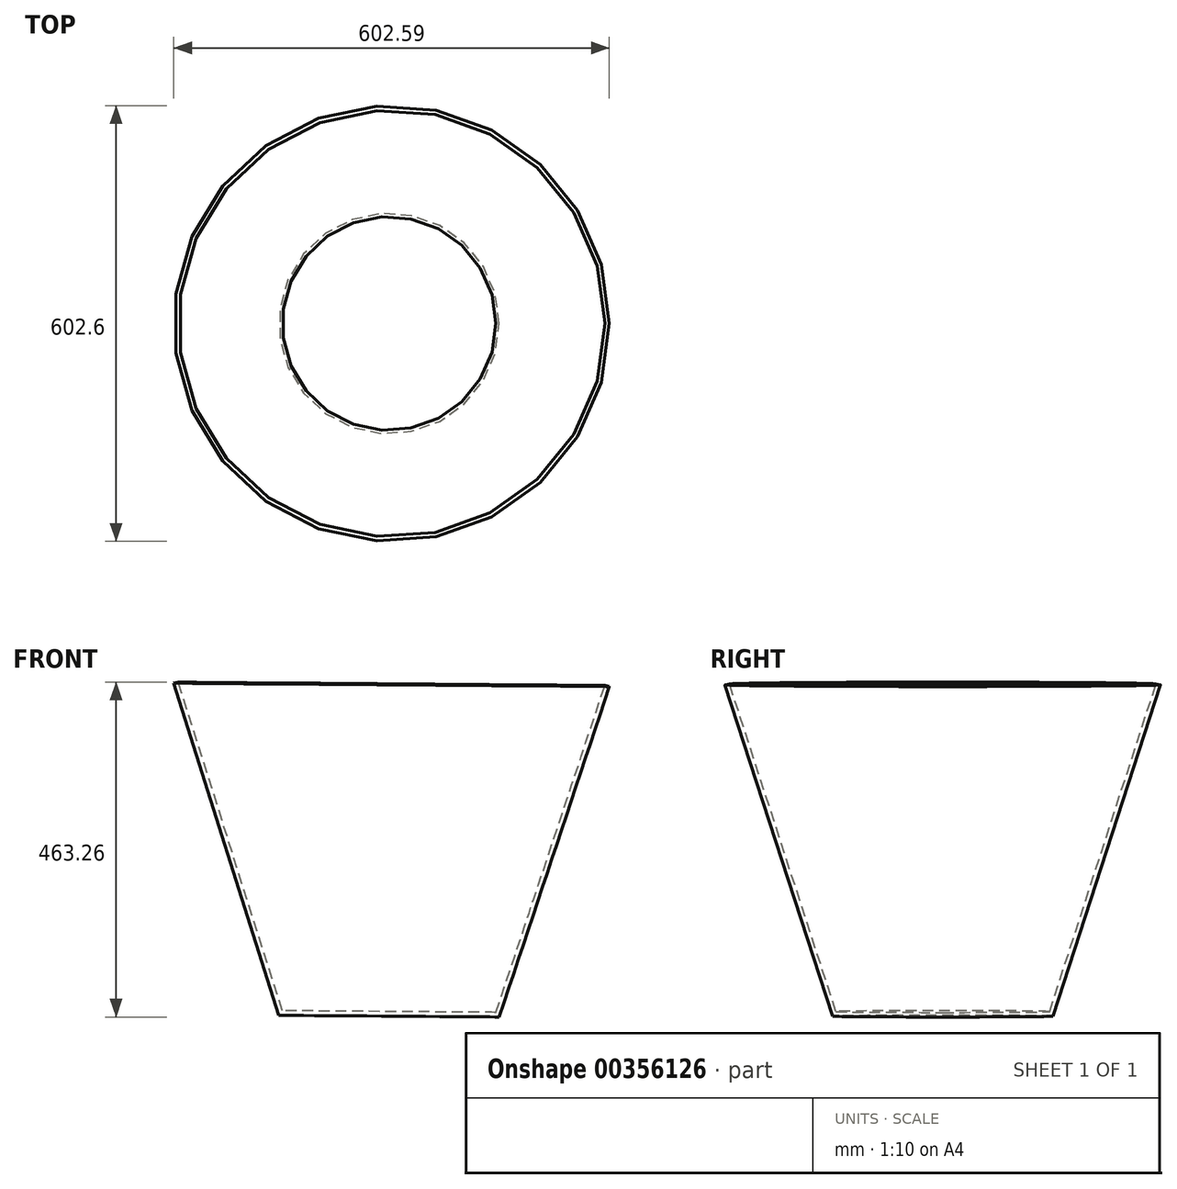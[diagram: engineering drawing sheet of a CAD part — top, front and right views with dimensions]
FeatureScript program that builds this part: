
annotation { "Feature Type Name" : "Feature", "Feature Type Description" : "" }
export const myFeature = defineFeature(function(context is Context, id is Id, definition is map)
    precondition{}
    {
        {
            var Q0;
            Q0=qCreatedBy(makeId("Front.planeOp"),FACE);
            var sketch = newSketch(context, id + "F0", { "sketchPlane" : qUnion([Q0])});
            skLineSegment(sketch, "E0", {"start": v(0, 0) * mm, "end": v(152.4, -1.17) * mm});
            skLineSegment(sketch, "E1", {"start": v(152.4, -1.17) * mm, "end": v(304.8, 456.03) * mm});
            skLineSegment(sketch, "E2.0", {"start": v(147.83, 5.22) * mm, "end": v(298.62, 457.58) * mm});
            skLineSegment(sketch, "E2.1", {"start": v(0.05, 6.35) * mm, "end": v(147.83, 5.22) * mm});
            skLineSegment(sketch, "E3", {"start": v(0.05, 6.35) * mm, "end": v(0, 0) * mm});
            skLineSegment(sketch, "E4", {"start": v(298.62, 457.58) * mm, "end": v(304.8, 456.03) * mm});
            skSolve(sketch);
        }
        {
            var Q0;
            Q0=makeQuery(id+"F0.imprint","IMPRINT",FACE,{"disambiguationData":[TD([[makeQuery(id+"F0.imprint","IMPRINT",EDGE,{"derivedFrom":sQuery(id+"F0.wireOp",EDGE,"E0")}),1.0]])]});
            var Q1;
            Q1=sQuery(id+"F0.wireOp",EDGE,"E3");
            revolve(context, id + "F1", {"entities" : qUnion([Q0]), "axis" : qUnion([Q1]), "revolveType" : RevolveType.FULL});
        }
    });
